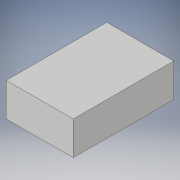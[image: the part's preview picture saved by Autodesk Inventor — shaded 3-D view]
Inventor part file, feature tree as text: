
AUTODESK INVENTOR PART (.ipt)
format: ipt  version: 2019 (Build 230136000, 136)  size: 86,528 bytes
history: native  units: mm
features: extrude x1, sketch x1
ambient origin geometry x8: Origin, YZ Plane, XZ Plane, XY Plane, X Axis, Y Axis, Z Axis, Center Point
bodies: Solid1 (feature_tree)
feature tree (2):
  extrude  "Extrusion1"  Depth=20.0mm
  sketch  "Sketch1"  dims[d0=30.0mm d1=20.0mm d2=10.0mm d3=0.0mm]
